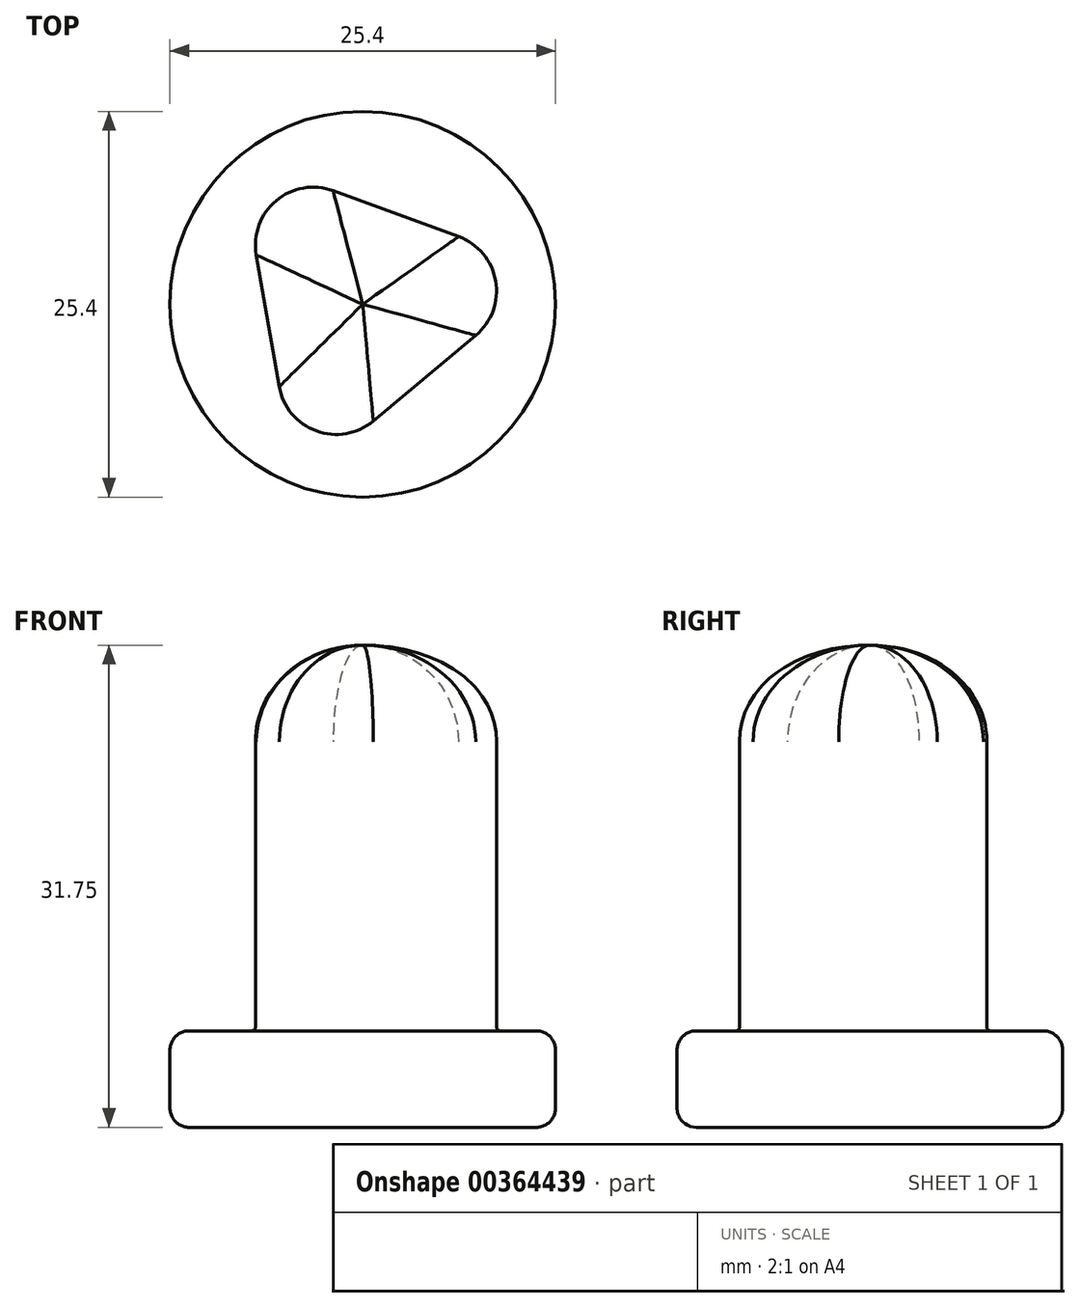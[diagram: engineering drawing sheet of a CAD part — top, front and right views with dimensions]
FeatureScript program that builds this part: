
annotation { "Feature Type Name" : "Feature", "Feature Type Description" : "" }
export const myFeature = defineFeature(function(context is Context, id is Id, definition is map)
    precondition{}
    {
        {
            var Q0;
            Q0=qCreatedBy(makeId("Top.planeOp"),FACE);
            var sketch = newSketch(context, id + "F0", { "sketchPlane" : qUnion([Q0])});
            skCircle(sketch, "E0", {"center": v(0, 0) * mm, "radius": 12.7 * mm});
            skSolve(sketch);
        }
        {
            var Q0;
            Q0=makeQuery(id+"F0.imprint","IMPRINT",FACE,{"disambiguationData":[TD([[makeQuery(id+"F0.imprint","IMPRINT",EDGE,{"derivedFrom":sQuery(id+"F0.wireOp",EDGE,"E0")}),1.0]])]});
            extrude(context, id + "F1", {"entities" : qUnion([Q0]), "depth" : 6.35 * mm});
        }
        {
            var Q0;
            Q0=makeQuery(id+"F1.opExtrude","CAP_FACE",FACE,{"disambiguationData":[OSD([sQuery(id+"F0.wireOp",EDGE,"E0")])],"isStart":false});
            var sketch = newSketch(context, id + "F2", { "sketchPlane" : qUnion([Q0])});
            skCircle(sketch, "E1.cCircle", {"center": v(0, 0) * mm, "radius": 12.7 * mm, "construction": true});
            skLineSegment(sketch, "E1.0", {"start": v(-8.14, 9.75) * mm, "end": v(12.51, 2.18) * mm});
            skLineSegment(sketch, "E1.1", {"start": v(12.51, 2.18) * mm, "end": v(-4.37, -11.93) * mm});
            skLineSegment(sketch, "E1.2", {"start": v(-4.37, -11.93) * mm, "end": v(-8.14, 9.75) * mm});
            skSolve(sketch);
        }
        {
            var Q0;
            Q0 = qSketchRegion(id + "F2", true);
            extrude(context, id + "F3", {"entities" : qUnion([Q0]), "operationType" : NewBodyOperationType.ADD, "depth" : 25.4 * mm});
        }
        {
            var Q0;
            Q0=makeQuery(id+"F3.opExtrude","SWEPT_EDGE",EDGE,{"disambiguationData":[OSD([sQuery(id+"F0.wireOp",EDGE,"E0"),sQuery(id+"F2.wireOp",EDGE,"E1.1"),sQuery(id+"F2.wireOp",EDGE,"E1.2")])]});
            var Q1;
            Q1=makeQuery(id+"F3.opExtrude","SWEPT_EDGE",EDGE,{"disambiguationData":[OSD([sQuery(id+"F0.wireOp",EDGE,"E0"),sQuery(id+"F2.wireOp",EDGE,"E1.0"),sQuery(id+"F2.wireOp",EDGE,"E1.1")])]});
            var Q2;
            Q2=makeQuery(id+"F3.opExtrude","SWEPT_EDGE",EDGE,{"disambiguationData":[OSD([sQuery(id+"F0.wireOp",EDGE,"E0"),sQuery(id+"F2.wireOp",EDGE,"E1.0"),sQuery(id+"F2.wireOp",EDGE,"E1.2")])]});
            fillet(context, id + "F4", {"entities" : qUnion([Q0, Q1, Q2]), "radius" : 3.8 * mm, "tangentPropagation" : true, "allowEdgeOverflow" : false});
        }
        {
            var Q0;
            {var subQ0=sQuery(id+"F2.wireOp",EDGE,"E1.2");var subQ1=sQuery(id+"F2.wireOp",EDGE,"E1.1");Q0=makeQuery(id+"F4.opFillet","BLEND_EDGE",EDGE,{"blendedFrom":[makeQuery(id+"F3.opExtrude","SWEPT_EDGE",EDGE,{"disambiguationData":[OSD([sQuery(id+"F0.wireOp",EDGE,"E0"),subQ1,subQ0])]}),makeQuery(id+"F3.opExtrude","CAP_FACE",FACE,{"disambiguationData":[OSD([sQuery(id+"F2.wireOp",EDGE,"E1.0"),subQ1,subQ0])],"isStart":false})],"blendedInto":[makeQuery(id+"F3.opExtrude","CAP_FACE",FACE,{"disambiguationData":[OSD([sQuery(id+"F2.wireOp",EDGE,"E1.0"),subQ1,subQ0])],"isStart":false})]});}
            var Q1;
            Q1=makeQuery(id+"F3.opExtrude","CAP_EDGE",EDGE,{"disambiguationData":[OSD([sQuery(id+"F2.wireOp",EDGE,"E1.1")])],"isStart":false});
            var Q2;
            Q2=makeQuery(id+"F3.opExtrude","CAP_EDGE",EDGE,{"disambiguationData":[OSD([sQuery(id+"F2.wireOp",EDGE,"E1.2")])],"isStart":false});
            var Q3;
            {var subQ0=sQuery(id+"F2.wireOp",EDGE,"E1.2");var subQ1=sQuery(id+"F2.wireOp",EDGE,"E1.0");Q3=makeQuery(id+"F4.opFillet","BLEND_EDGE",EDGE,{"blendedFrom":[makeQuery(id+"F3.opExtrude","SWEPT_EDGE",EDGE,{"disambiguationData":[OSD([sQuery(id+"F0.wireOp",EDGE,"E0"),subQ1,subQ0])]}),makeQuery(id+"F3.opExtrude","CAP_FACE",FACE,{"disambiguationData":[OSD([subQ1,sQuery(id+"F2.wireOp",EDGE,"E1.1"),subQ0])],"isStart":false})],"blendedInto":[makeQuery(id+"F3.opExtrude","CAP_FACE",FACE,{"disambiguationData":[OSD([subQ1,sQuery(id+"F2.wireOp",EDGE,"E1.1"),subQ0])],"isStart":false})]});}
            var Q4;
            Q4=makeQuery(id+"F3.opExtrude","CAP_EDGE",EDGE,{"disambiguationData":[OSD([sQuery(id+"F2.wireOp",EDGE,"E1.0")])],"isStart":false});
            var Q5;
            {var subQ0=sQuery(id+"F2.wireOp",EDGE,"E1.1");var subQ1=sQuery(id+"F2.wireOp",EDGE,"E1.0");Q5=makeQuery(id+"F4.opFillet","BLEND_EDGE",EDGE,{"blendedFrom":[makeQuery(id+"F3.opExtrude","SWEPT_EDGE",EDGE,{"disambiguationData":[OSD([sQuery(id+"F0.wireOp",EDGE,"E0"),subQ1,subQ0])]}),makeQuery(id+"F3.opExtrude","CAP_FACE",FACE,{"disambiguationData":[OSD([subQ1,subQ0,sQuery(id+"F2.wireOp",EDGE,"E1.2")])],"isStart":false})],"blendedInto":[makeQuery(id+"F3.opExtrude","CAP_FACE",FACE,{"disambiguationData":[OSD([subQ1,subQ0,sQuery(id+"F2.wireOp",EDGE,"E1.2")])],"isStart":false})]});}
            fillet(context, id + "F5", {"entities" : qUnion([Q0, Q1, Q2, Q3, Q4, Q5]), "radius" : 6.35 * mm, "tangentPropagation" : true, "allowEdgeOverflow" : false});
        }
        {
            var Q0;
            Q0=makeQuery(id+"F3.boolean.opBoolean","SPLIT",EDGE,{"disambiguationData":[OD(0.0)],"derivedFrom":makeQuery(id+"F1.opExtrude","CAP_EDGE",EDGE,{"disambiguationData":[OSD([sQuery(id+"F0.wireOp",EDGE,"E0")])],"isStart":false})});
            var Q1;
            Q1=makeQuery(id+"F3.boolean.opBoolean","SPLIT",EDGE,{"disambiguationData":[OD(2.0)],"derivedFrom":makeQuery(id+"F1.opExtrude","CAP_EDGE",EDGE,{"disambiguationData":[OSD([sQuery(id+"F0.wireOp",EDGE,"E0")])],"isStart":false})});
            var Q2;
            Q2=makeQuery(id+"F3.boolean.opBoolean","SPLIT",EDGE,{"disambiguationData":[OD(1.0)],"derivedFrom":makeQuery(id+"F1.opExtrude","CAP_EDGE",EDGE,{"disambiguationData":[OSD([sQuery(id+"F0.wireOp",EDGE,"E0")])],"isStart":false})});
            var Q3;
            Q3=makeQuery(id+"F1.opExtrude","CAP_EDGE",EDGE,{"disambiguationData":[OSD([sQuery(id+"F0.wireOp",EDGE,"E0")])],"isStart":true});
            fillet(context, id + "F6", {"entities" : qUnion([Q0, Q1, Q2, Q3]), "radius" : 1.27 * mm, "tangentPropagation" : true, "allowEdgeOverflow" : false});
        }
        {
            var Q0;
            Q0=makeQuery(id+"F3.opExtrude","CAP_EDGE",EDGE,{"disambiguationData":[OSD([sQuery(id+"F2.wireOp",EDGE,"E1.1")])],"isStart":true});
            var Q1;
            {var subQ0=sQuery(id+"F0.wireOp",EDGE,"E0");var subQ1=makeQuery(id+"F1.opExtrude","CAP_FACE",FACE,{"disambiguationData":[OSD([subQ0])],"isStart":false});Q1=makeQuery(id+"F4.opFillet","BLEND_EDGE",EDGE,{"blendedFrom":[makeQuery(id+"F3.opExtrude","SWEPT_EDGE",EDGE,{"disambiguationData":[OSD([subQ0,sQuery(id+"F2.wireOp",EDGE,"E1.0"),sQuery(id+"F2.wireOp",EDGE,"E1.1")])]}),makeQuery(id+"F3.boolean.opBoolean","SPLIT",FACE,{"disambiguationData":[OD(0.0)],"derivedFrom":subQ1}),makeQuery(id+"F3.boolean.opBoolean","SPLIT",FACE,{"disambiguationData":[OD(1.0)],"derivedFrom":subQ1}),makeQuery(id+"F3.boolean.opBoolean","SPLIT",FACE,{"disambiguationData":[OD(2.0)],"derivedFrom":subQ1})],"blendedInto":[makeQuery(id+"F3.boolean.opBoolean","SPLIT",FACE,{"disambiguationData":[OD(0.0)],"derivedFrom":subQ1}),makeQuery(id+"F3.boolean.opBoolean","SPLIT",FACE,{"disambiguationData":[OD(1.0)],"derivedFrom":subQ1}),makeQuery(id+"F3.boolean.opBoolean","SPLIT",FACE,{"disambiguationData":[OD(2.0)],"derivedFrom":subQ1})]});}
            var Q2;
            Q2=makeQuery(id+"F3.opExtrude","CAP_EDGE",EDGE,{"disambiguationData":[OSD([sQuery(id+"F2.wireOp",EDGE,"E1.0")])],"isStart":true});
            var Q3;
            {var subQ0=sQuery(id+"F0.wireOp",EDGE,"E0");var subQ1=makeQuery(id+"F1.opExtrude","CAP_FACE",FACE,{"disambiguationData":[OSD([subQ0])],"isStart":false});Q3=makeQuery(id+"F4.opFillet","BLEND_EDGE",EDGE,{"blendedFrom":[makeQuery(id+"F3.opExtrude","SWEPT_EDGE",EDGE,{"disambiguationData":[OSD([subQ0,sQuery(id+"F2.wireOp",EDGE,"E1.0"),sQuery(id+"F2.wireOp",EDGE,"E1.2")])]}),makeQuery(id+"F3.boolean.opBoolean","SPLIT",FACE,{"disambiguationData":[OD(0.0)],"derivedFrom":subQ1}),makeQuery(id+"F3.boolean.opBoolean","SPLIT",FACE,{"disambiguationData":[OD(1.0)],"derivedFrom":subQ1}),makeQuery(id+"F3.boolean.opBoolean","SPLIT",FACE,{"disambiguationData":[OD(2.0)],"derivedFrom":subQ1})],"blendedInto":[makeQuery(id+"F3.boolean.opBoolean","SPLIT",FACE,{"disambiguationData":[OD(0.0)],"derivedFrom":subQ1}),makeQuery(id+"F3.boolean.opBoolean","SPLIT",FACE,{"disambiguationData":[OD(1.0)],"derivedFrom":subQ1}),makeQuery(id+"F3.boolean.opBoolean","SPLIT",FACE,{"disambiguationData":[OD(2.0)],"derivedFrom":subQ1})]});}
            var Q4;
            {var subQ0=sQuery(id+"F0.wireOp",EDGE,"E0");var subQ1=makeQuery(id+"F1.opExtrude","CAP_FACE",FACE,{"disambiguationData":[OSD([subQ0])],"isStart":false});Q4=makeQuery(id+"F4.opFillet","BLEND_EDGE",EDGE,{"blendedFrom":[makeQuery(id+"F3.opExtrude","SWEPT_EDGE",EDGE,{"disambiguationData":[OSD([subQ0,sQuery(id+"F2.wireOp",EDGE,"E1.1"),sQuery(id+"F2.wireOp",EDGE,"E1.2")])]}),makeQuery(id+"F3.boolean.opBoolean","SPLIT",FACE,{"disambiguationData":[OD(0.0)],"derivedFrom":subQ1}),makeQuery(id+"F3.boolean.opBoolean","SPLIT",FACE,{"disambiguationData":[OD(1.0)],"derivedFrom":subQ1}),makeQuery(id+"F3.boolean.opBoolean","SPLIT",FACE,{"disambiguationData":[OD(2.0)],"derivedFrom":subQ1})],"blendedInto":[makeQuery(id+"F3.boolean.opBoolean","SPLIT",FACE,{"disambiguationData":[OD(0.0)],"derivedFrom":subQ1}),makeQuery(id+"F3.boolean.opBoolean","SPLIT",FACE,{"disambiguationData":[OD(1.0)],"derivedFrom":subQ1}),makeQuery(id+"F3.boolean.opBoolean","SPLIT",FACE,{"disambiguationData":[OD(2.0)],"derivedFrom":subQ1})]});}
            var Q5;
            Q5=makeQuery(id+"F3.opExtrude","CAP_EDGE",EDGE,{"disambiguationData":[OSD([sQuery(id+"F2.wireOp",EDGE,"E1.2")])],"isStart":true});
            fillet(context, id + "F7", {"entities" : qUnion([Q0, Q1, Q2, Q3, Q4, Q5]), "radius" : 0.25 * mm, "tangentPropagation" : true, "allowEdgeOverflow" : false});
        }
    });
